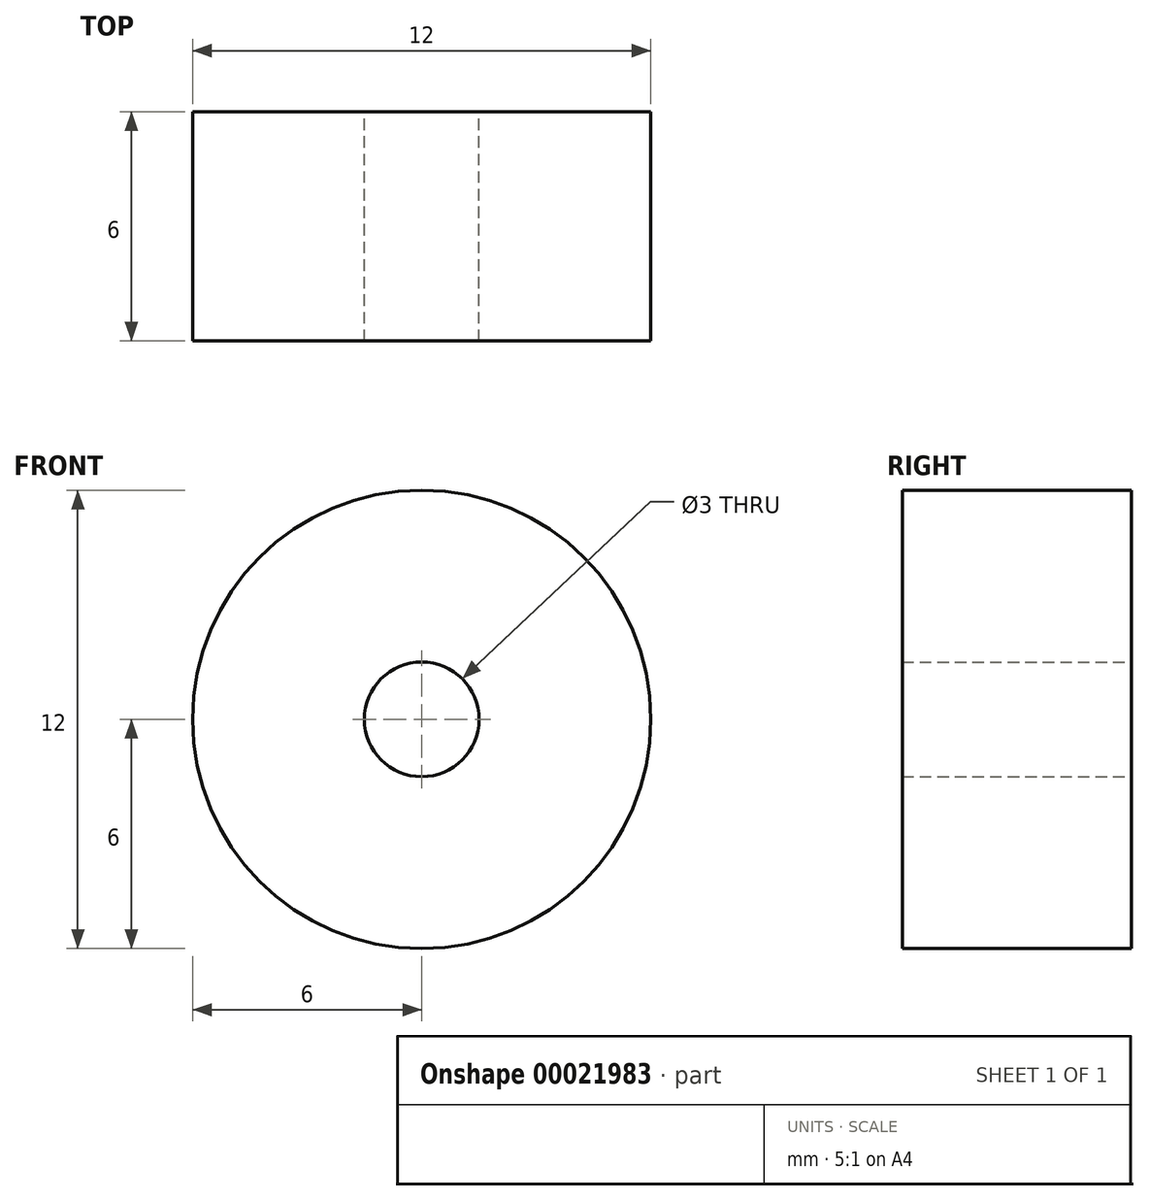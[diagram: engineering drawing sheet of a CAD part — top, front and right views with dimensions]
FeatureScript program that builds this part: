
annotation { "Feature Type Name" : "Feature", "Feature Type Description" : "" }
export const myFeature = defineFeature(function(context is Context, id is Id, definition is map)
    precondition{}
    {
        {
            var Q0;
            Q0=qCreatedBy(makeId("Front.planeOp"),FACE);
            var sketch = newSketch(context, id + "F0", { "sketchPlane" : qUnion([Q0])});
            skCircle(sketch, "E0", {"center": v(0, 0) * mm, "radius": 6 * mm});
            skSolve(sketch);
        }
        {
            var Q0;
            Q0=makeQuery(id+"F0.imprint","IMPRINT",FACE,{"disambiguationData":[TD([[makeQuery(id+"F0.imprint","IMPRINT",EDGE,{"derivedFrom":sQuery(id+"F0.wireOp",EDGE,"E0")}),1.0]])]});
            extrude(context, id + "F1", {"entities" : qUnion([Q0]), "depth" : 6 * mm});
        }
        {
            var Q0;
            Q0=sQuery(id+"F0.wireOp",VERTEX,"E0.center");
            var Q1;
            Q1=makeQuery(id+"F1.opExtrude","SWEPT_BODY",BODY,{"disambiguationData":[OSD([sQuery(id+"F0.wireOp",EDGE,"E0")])]});
            hole(context, id + "F2", {"style" : HoleStyle.SIMPLE, "holeDiameter" : 3 * mm, "endStyle" : HoleEndStyle.THROUGH, "oppositeDirection" : true, "locations" : qUnion([Q0]), "scope" : qUnion([Q1])});
        }
    });
